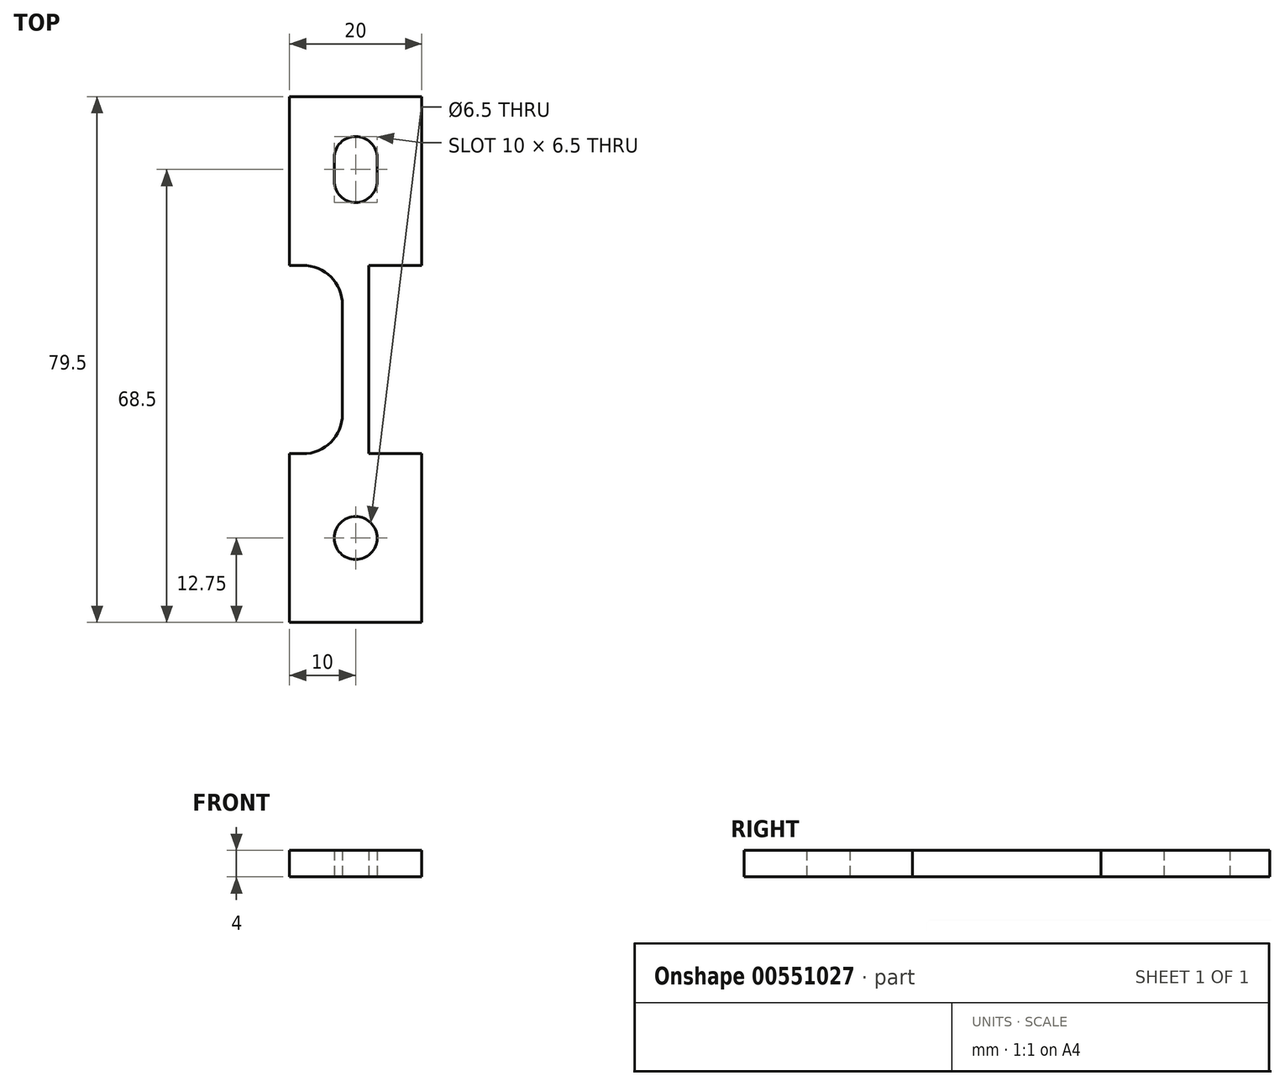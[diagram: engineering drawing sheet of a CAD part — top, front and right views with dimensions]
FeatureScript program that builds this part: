
annotation { "Feature Type Name" : "Feature", "Feature Type Description" : "" }
export const myFeature = defineFeature(function(context is Context, id is Id, definition is map)
    precondition{}
    {
        {
            var Q0;
            Q0=qCreatedBy(makeId("Top.planeOp"),FACE);
            var sketch = newSketch(context, id + "F0", { "sketchPlane" : qUnion([Q0])});
            skLineSegment(sketch, "E0.bottom", {"start": v(-10, 39.75) * mm, "end": v(10, 39.75) * mm});
            skLineSegment(sketch, "E0.top", {"start": v(-10, 14.25) * mm, "end": v(10, 14.25) * mm});
            skLineSegment(sketch, "E0.left", {"start": v(-10, 39.75) * mm, "end": v(-10, 14.25) * mm});
            skLineSegment(sketch, "E0.right", {"start": v(10, 39.75) * mm, "end": v(10, 14.25) * mm});
            skLineSegment(sketch, "E1", {"start": v(0, 30.5) * mm, "end": v(0, 27) * mm, "construction": true});
            skPoint(sketch, "E1.endSnap0", {"position": v(0, 28.75) * mm});
            skArc(sketch, "E2.0.startCap", {"start": v(-3.25, 30.5) * mm, "mid": v(0, 33.75) * mm, "end": v(3.25, 30.5) * mm});
            skArc(sketch, "E2.0.endCap", {"start": v(3.25, 27) * mm, "mid": v(0, 23.75) * mm, "end": v(-3.25, 27) * mm});
            skLineSegment(sketch, "E2.0.left", {"start": v(3.25, 30.5) * mm, "end": v(3.25, 27) * mm});
            skLineSegment(sketch, "E2.0.right", {"start": v(-3.25, 30.5) * mm, "end": v(-3.25, 27) * mm});
            skCircle(sketch, "E3", {"center": v(0, -27) * mm, "radius": 3.25 * mm});
            skLineSegment(sketch, "E4.bottom", {"start": v(-10, -39.75) * mm, "end": v(10, -39.75) * mm});
            skLineSegment(sketch, "E4.top", {"start": v(-10, -14.25) * mm, "end": v(10, -14.25) * mm});
            skLineSegment(sketch, "E4.left", {"start": v(-10, -39.75) * mm, "end": v(-10, -14.25) * mm});
            skLineSegment(sketch, "E4.right", {"start": v(10, -39.75) * mm, "end": v(10, -14.25) * mm});
            skLineSegment(sketch, "E5", {"start": v(-10, -39.75) * mm, "end": v(10, -14.25) * mm, "construction": true});
            skLineSegment(sketch, "E6", {"start": v(0, 23.75) * mm, "end": v(0, 0) * mm, "construction": true});
            skLineSegment(sketch, "E7", {"start": v(0, 0) * mm, "end": v(0, -23.75) * mm, "construction": true});
            skLineSegment(sketch, "E8", {"start": v(0, 23.75) * mm, "end": v(-10, 23.75) * mm, "construction": true});
            skLineSegment(sketch, "E9", {"start": v(-10, 23.75) * mm, "end": v(-10, 14.25) * mm, "construction": true});
            skLineSegment(sketch, "E10", {"start": v(0, -23.75) * mm, "end": v(-10, -23.75) * mm, "construction": true});
            skLineSegment(sketch, "E11", {"start": v(-10, -23.75) * mm, "end": v(-10, -14.25) * mm, "construction": true});
            skSolve(sketch);
        }
        {
            var Q0;
            Q0=qSketchRegion(id+"F0",true);
            extrude(context, id + "F1", {"entities" : qUnion([Q0]), "depth" : 4 * mm});
        }
        {
            var Q0;
            Q0=qCreatedBy(makeId("Top.planeOp"),FACE);
            var sketch = newSketch(context, id + "F2", { "sketchPlane" : qUnion([Q0])});
            skLineSegment(sketch, "E12.bottom", {"start": v(-2, 14.25) * mm, "end": v(2, 14.25) * mm});
            skLineSegment(sketch, "E12.top", {"start": v(-2, -14.25) * mm, "end": v(2, -14.25) * mm});
            skLineSegment(sketch, "E12.left", {"start": v(-2, 14.25) * mm, "end": v(-2, -14.25) * mm});
            skLineSegment(sketch, "E12.right", {"start": v(2, 14.25) * mm, "end": v(2, -14.25) * mm});
            skLineSegment(sketch, "E13", {"start": v(0, 14.25) * mm, "end": v(0, -14.25) * mm, "construction": true});
            skSolve(sketch);
        }
        {
            var Q0;
            Q0=qSketchRegion(id+"F2",true);
            extrude(context, id + "F3", {"entities" : qUnion([Q0]), "operationType" : NewBodyOperationType.ADD, "depth" : 4 * mm});
        }
        {
            var Q0;
            Q0=makeQuery(id+"F3.opExtrude","SWEPT_EDGE",EDGE,{"disambiguationData":[OSD([sQuery(id+"F2.wireOp",EDGE,"E12.bottom"),sQuery(id+"F2.wireOp",EDGE,"E12.left")])]});
            var Q1;
            Q1=makeQuery(id+"F3.opExtrude","SWEPT_EDGE",EDGE,{"disambiguationData":[OSD([sQuery(id+"F2.wireOp",EDGE,"E12.bottom"),sQuery(id+"F2.wireOp",EDGE,"E12.right")])]});
            var Q2;
            Q2=makeQuery(id+"F3.opExtrude","SWEPT_EDGE",EDGE,{"disambiguationData":[OSD([sQuery(id+"F2.wireOp",EDGE,"E12.top"),sQuery(id+"F2.wireOp",EDGE,"E12.right")])]});
            var Q3;
            Q3=makeQuery(id+"F3.opExtrude","SWEPT_EDGE",EDGE,{"disambiguationData":[OSD([sQuery(id+"F2.wireOp",EDGE,"E12.top"),sQuery(id+"F2.wireOp",EDGE,"E12.left")])]});
            fillet(context, id + "F4", {"entities" : qUnion([Q0, Q1, Q2, Q3]), "radius" : 6 * mm, "tangentPropagation" : true, "allowEdgeOverflow" : false});
        }
    });
